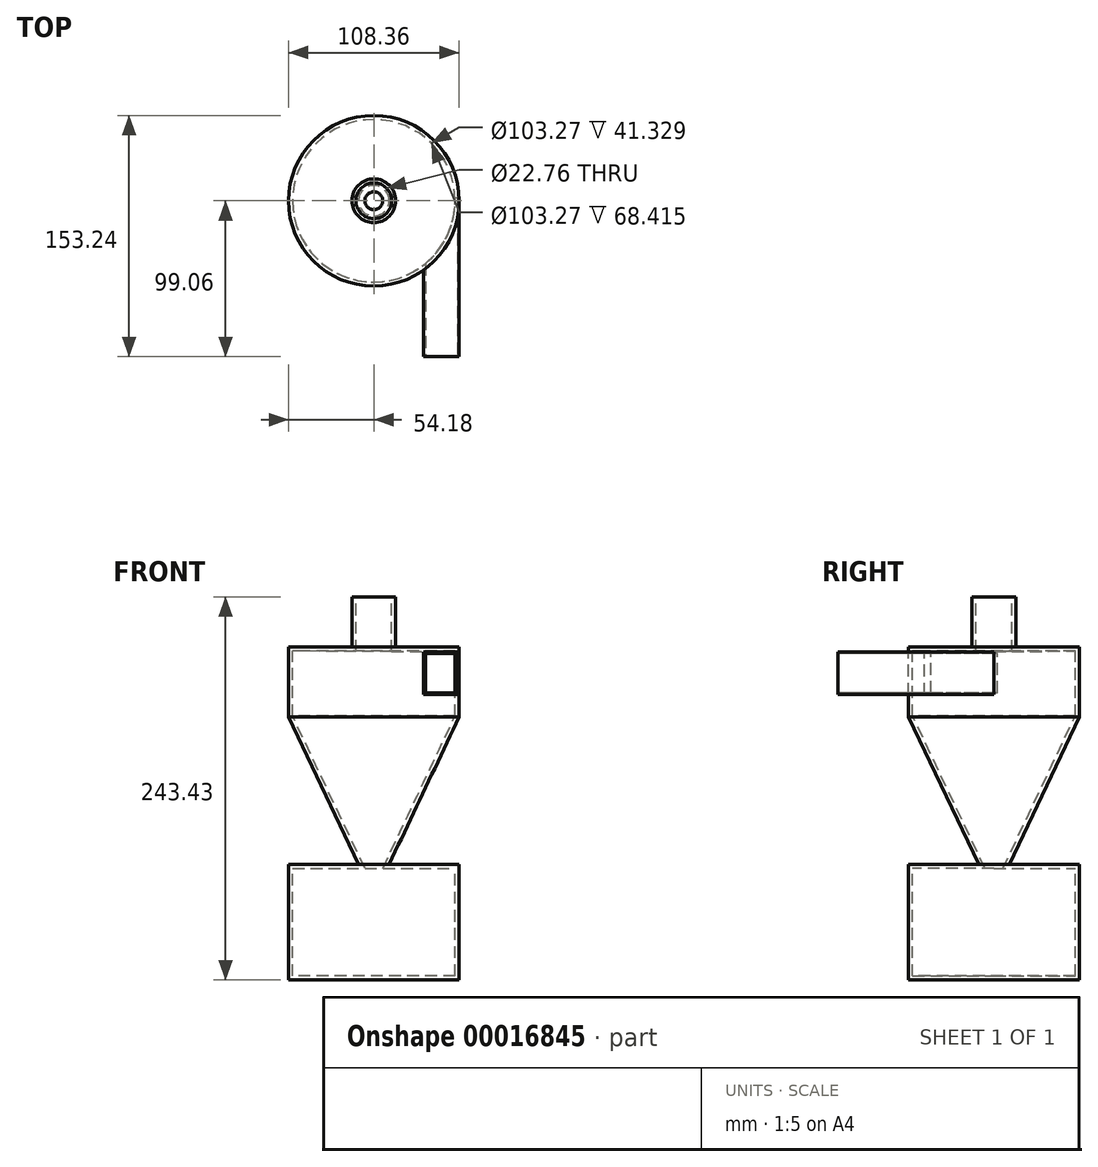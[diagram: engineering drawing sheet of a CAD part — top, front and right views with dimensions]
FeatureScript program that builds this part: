
annotation { "Feature Type Name" : "Feature", "Feature Type Description" : "" }
export const myFeature = defineFeature(function(context is Context, id is Id, definition is map)
    precondition{}
    {
        {
            var Q0;
            Q0=qCreatedBy(makeId("Front.planeOp"),FACE);
            var sketch = newSketch(context, id + "F0", { "sketchPlane" : qUnion([Q0])});
            skLineSegment(sketch, "E0", {"start": v(0, 107.5) * mm, "end": v(0, -135.92) * mm});
            skLineSegment(sketch, "E1", {"start": v(0, -135.92) * mm, "end": v(-54.18, -135.92) * mm});
            skLineSegment(sketch, "E2", {"start": v(-54.18, -135.92) * mm, "end": v(-54.18, -62.42) * mm});
            skLineSegment(sketch, "E3", {"start": v(-54.18, -62.42) * mm, "end": v(-9.7, -62.42) * mm});
            skLineSegment(sketch, "E4", {"start": v(-9.7, -62.42) * mm, "end": v(-54.18, 31.2) * mm});
            skLineSegment(sketch, "E5", {"start": v(-54.18, 31.2) * mm, "end": v(-54.18, 75.67) * mm});
            skLineSegment(sketch, "E6", {"start": v(-54.18, 75.67) * mm, "end": v(-13.92, 75.2) * mm});
            skLineSegment(sketch, "E7", {"start": v(-13.92, 75.2) * mm, "end": v(-13.92, 107.5) * mm});
            skLineSegment(sketch, "E8", {"start": v(-13.92, 107.5) * mm, "end": v(0.13, 107.04) * mm});
            skSolve(sketch);
        }
        {
            var Q0;
            Q0=qSketchRegion(id+"F0",true);
            var Q1;
            Q1=sQuery(id+"F0.wireOp",EDGE,"E0");
            revolve(context, id + "F1", {"entities" : qUnion([Q0]), "axis" : qUnion([Q1]), "revolveType" : RevolveType.FULL});
        }
        {
            var Q0;
            Q0=makeQuery(id+"F1.opRevolve","SWEPT_FACE",FACE,{"disambiguationData":[OSD([sQuery(id+"F0.wireOp",EDGE,"E8")])]});
            shell(context, id + "F2", {"entities" : qUnion([Q0]), "thickness" : 2.54 * mm});
        }
        {
            var Q0;
            Q0=qCreatedBy(makeId("Front.planeOp"),FACE);
            var sketch = newSketch(context, id + "F3", { "sketchPlane" : qUnion([Q0])});
            skLineSegment(sketch, "E9.bottom", {"start": v(54.11, 72.35) * mm, "end": v(44.53, 72.35) * mm});
            skLineSegment(sketch, "E9.top", {"start": v(54.11, 50.67) * mm, "end": v(44.53, 50.67) * mm});
            skLineSegment(sketch, "E9.left", {"start": v(54.11, 72.35) * mm, "end": v(54.11, 50.67) * mm});
            skLineSegment(sketch, "E9.right", {"start": v(44.53, 72.35) * mm, "end": v(44.53, 50.67) * mm});
            skSolve(sketch);
        }
        {
            var Q0;
            Q0=qSketchRegion(id+"F3",true);
            extrude(context, id + "F4", {"entities" : qUnion([Q0]), "operationType" : NewBodyOperationType.REMOVE, "depth" : 58.58 * mm});
        }
        {
            var Q0;
            Q0=qCreatedBy(makeId("Front.planeOp"),FACE);
            var sketch = newSketch(context, id + "F5", { "sketchPlane" : qUnion([Q0])});
            skLineSegment(sketch, "E10.bottom", {"start": v(54.18, 72.6) * mm, "end": v(31.52, 72.6) * mm});
            skLineSegment(sketch, "E10.top", {"start": v(54.18, 45.43) * mm, "end": v(31.52, 45.43) * mm});
            skLineSegment(sketch, "E10.left", {"start": v(54.18, 72.6) * mm, "end": v(54.18, 45.43) * mm});
            skLineSegment(sketch, "E10.right", {"start": v(31.52, 72.6) * mm, "end": v(31.52, 45.43) * mm});
            skSolve(sketch);
        }
        {
            var Q0;
            Q0=qSketchRegion(id+"F5",true);
            extrude(context, id + "F6", {"entities" : qUnion([Q0]), "operationType" : NewBodyOperationType.ADD, "depth" : 101.6 * mm});
        }
        {
            var Q0;
            {var subQ0=sQuery(id+"F5.wireOp",EDGE,"E10.bottom");var subQ6=sQuery(id+"F0.wireOp",EDGE,"E5");var subQ9=makeQuery(id+"F2.opShell","OFFSET_FACE",FACE,{"disambiguationData":[OSD([subQ6])]});Q0=makeQuery(id+"F6.boolean.opBoolean","SPLIT",FACE,{"disambiguationData":[TD([subQ9])],"derivedFrom":makeQuery(id+"F6.opExtrude","SWEPT_FACE",FACE,{"disambiguationData":[OSD([subQ0])]})});}
            extrude(context, id + "F7", {"entities" : qUnion([Q0]), "operationType" : NewBodyOperationType.REMOVE, "oppositeDirection" : true, "depth" : 29.38 * mm});
        }
        {
            var Q0;
            Q0=makeQuery(id+"F6.opExtrude","CAP_FACE",FACE,{"disambiguationData":[OSD([sQuery(id+"F5.wireOp",EDGE,"E10.bottom"),sQuery(id+"F5.wireOp",EDGE,"E10.top"),sQuery(id+"F5.wireOp",EDGE,"E10.left"),sQuery(id+"F5.wireOp",EDGE,"E10.right")])],"isStart":false});
            var sketch = newSketch(context, id + "F8", { "sketchPlane" : qUnion([Q0])});
            skLineSegment(sketch, "E11.bottom", {"start": v(32.68, 71.46) * mm, "end": v(53, 71.46) * mm});
            skLineSegment(sketch, "E11.top", {"start": v(32.68, 46.43) * mm, "end": v(53, 46.43) * mm});
            skLineSegment(sketch, "E11.left", {"start": v(32.68, 71.46) * mm, "end": v(32.68, 46.43) * mm});
            skLineSegment(sketch, "E11.right", {"start": v(53, 71.46) * mm, "end": v(53, 46.43) * mm});
            skSolve(sketch);
        }
        {
            var Q0;
            Q0=qSketchRegion(id+"F8",true);
            var Q1;
            Q1=makeQuery(id+"F8.imprint","IMPRINT",FACE,{"disambiguationData":[TD([[makeQuery(id+"F8.imprint","IMPRINT",EDGE,{"derivedFrom":makeQuery(id+"F6.opExtrude","CAP_EDGE",EDGE,{"disambiguationData":[OSD([sQuery(id+"F5.wireOp",EDGE,"E10.bottom")])],"isStart":false})}),1.0]])]});
            extrude(context, id + "F9", {"entities" : qUnion([Q0, Q1]), "operationType" : NewBodyOperationType.REMOVE, "oppositeDirection" : true, "depth" : 2.54 * mm});
        }
        {
            var Q0;
            Q0 = qSketchRegion(id + "F8", true);
            extrude(context, id + "F10", {"entities" : qUnion([Q0]), "operationType" : NewBodyOperationType.REMOVE, "oppositeDirection" : true, "depth" : 103.65 * mm});
        }
    });
